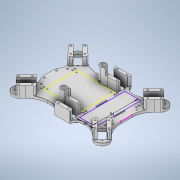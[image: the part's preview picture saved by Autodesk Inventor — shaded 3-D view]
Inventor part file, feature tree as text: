
AUTODESK INVENTOR PART (.ipt)
format: ipt  version: 2020.3 (Build 243373000, 373)  size: 1,457,664 bytes
history: native  units: mm
features: sketch x9, extrude x9, fillet x8, hole x7, projected_geometry x2, plane x1
ambient origin geometry x8: Origin, YZ Plane, XZ Plane, XY Plane, X Axis, Y Axis, Z Axis, Center Point
bodies: Body1 (feature_tree)
feature tree (36):
  sketch  "Sketch1"  dims[d0=135.0deg d4=24.6mm]
  extrude  "Extrusion10"  Depth=24.6mm
  extrude  "Extrusion11"  Depth=70.0mm
  extrude  "Extrusion12"  Depth=8.7mm
  sketch  "Sketch12"  dims[d53=1.5mm d54=20.0mm d59=1.0mm d60=90.0mm d61=135.0deg d70=135.0deg d82=0.7mm d83=0.7mm d84=0.7mm d85=0.7mm d86=6.0mm d87=5.0mm d88=0.0mm d89=20.92mm d90=0.0mm d91=1.9mm d92=6.0mm d93=4.2mm d94=2.0mm d95=90.0deg d96=8.0mm d97=0.0mm d98=2.0mm d99=1.0mm d100=2.0mm d101=0.5mm d103=0.5mm d104=0.5mm d105=18.0mm d108=3.0mm d110=2.9mm d111=6.0mm d112=4.0mm d113=2.0mm d114=90.0deg d115=4.3mm d116=0.0mm d117=30.0mm d119=84.0mm d120=1.9mm d121=6.0mm d122=4.0mm d123=2.0mm d124=90.0deg d125=8.0mm d126=0.0mm d128=12.0mm d129=2.094395mm d130=6.0mm d134=32.32mm d135=0.0mm d136=0.3mm d137=5.6mm d138=6.0mm d139=9.0mm d140=1.1mm d141=90.0deg d142=6.6mm d143=0.0mm d144=0.2mm d145=1.0mm d146=1.5mm d147=10.0mm d148=0.0mm d149=0.0mm d150=1.0mm d151=10.0mm d152=1.5mm d153=10.0mm d154=0.0mm d155=1.0mm d156=10.0mm d158=1.5mm d159=10.0mm d160=0.0mm d161=1.0mm d162=10.0mm d163=1.5mm d164=10.0mm d165=0.0mm d166=2.0mm d173=0.5mm d174=4.0mm d175=1.0mm d176=3.0mm d177=0.5mm d178=9.7mm d179=4.0mm d181=0.2mm d182=6.0mm d183=4.0mm d185=21.842mm d186=0.0mm d187=0.3mm d188=24.0mm d189=52.462385mm d190=74.962385mm d191=2.0mm d192=2.0mm d193=2.0mm d194=2.1mm d195=6.0mm d196=4.0mm d197=2.0mm d198=90.0deg d199=7.3mm d200=0.0mm d201=10.0mm d204=30.0deg d205=25.0mm d206=5.0mm d207=0.0mm d210=15.0mm d211=10.0mm d213=15.0mm d214=4.0mm d215=22.856406mm d216=3.0mm d217=45.0mm d218=3.0mm d219=6.0mm d220=6.5mm d221=2.0mm d222=90.0deg d223=8.0mm d224=20.594885mm d225=3.0mm d226=6.0mm d227=6.5mm d228=2.0mm d229=90.0deg d230=8.0mm d231=20.594885mm]
  extrude  "Extrusion19"  Depth=6.0mm
  hole  "Hole1"  [1 undecoded]
  fillet  "Fillet8"  Radius=20.0mm
  fillet  "Fillet9"  Radius=6.0mm
  fillet  "Fillet11"  Radius=135.0mm
  fillet  "Fillet12"  Radius=15.0mm
  fillet  "Fillet14"  Radius=4.0mm
  sketch  "Sketch2"  dims[d5=12.4mm d6=70.0mm]
  hole  "Hole2"  [1 undecoded]
  sketch  "Sketch3"  dims[d7=60.0mm d9=8.7mm]
  hole  "Hole3"  [1 undecoded]
  fillet  "Fillet13"  Radius=84.0mm
  extrude  "Extrusion13"  Depth=3.0mm
  extrude  "Extrusion14"  Depth=10.0mm
  extrude  "Extrusion15"  Depth=10.0mm
  extrude  "Extrusion16"  Depth=10.0mm
  plane  "Work Plane1"
  hole  "Hole4"  [1 undecoded]
  extrude  "Extrusion18"  TaperAngle=135.0deg  [1 undecoded]
  fillet  "Fillet15"  Radius=0.7mm
  fillet  "Fillet16"  Radius=0.7mm
  hole  "Hole5"  [1 undecoded]
  sketch  "Sketch11"  dims[d51=3.0mm d52=3.0mm]
  hole  "Hole6"  [1 undecoded]
  hole  "Hole7"  [1 undecoded]
  sketch  "Sketch4"  dims[d10=135.0deg d12=6.0mm]
  sketch  "Sketch6"  dims[d13=2.0mm d14=2.0mm d16=20.0mm d23=6.0mm d29=135.0mm d32=15.0mm d33=4.0mm]
  projected_geometry  "Projected Loop1"
  sketch  "Sketch8"  dims[d34=28.4mm d38=4.0mm]
  sketch  "Sketch10"  dims[d40=6.8mm d49=30.0mm d50=84.0mm]
  projected_geometry  "Project Cut Edges4"
note: 8 required parameter values undecoded (feature->parameter linkage not recoverable at this tier; creation-order binding heuristic only, values carry confidence <= 0.55)
